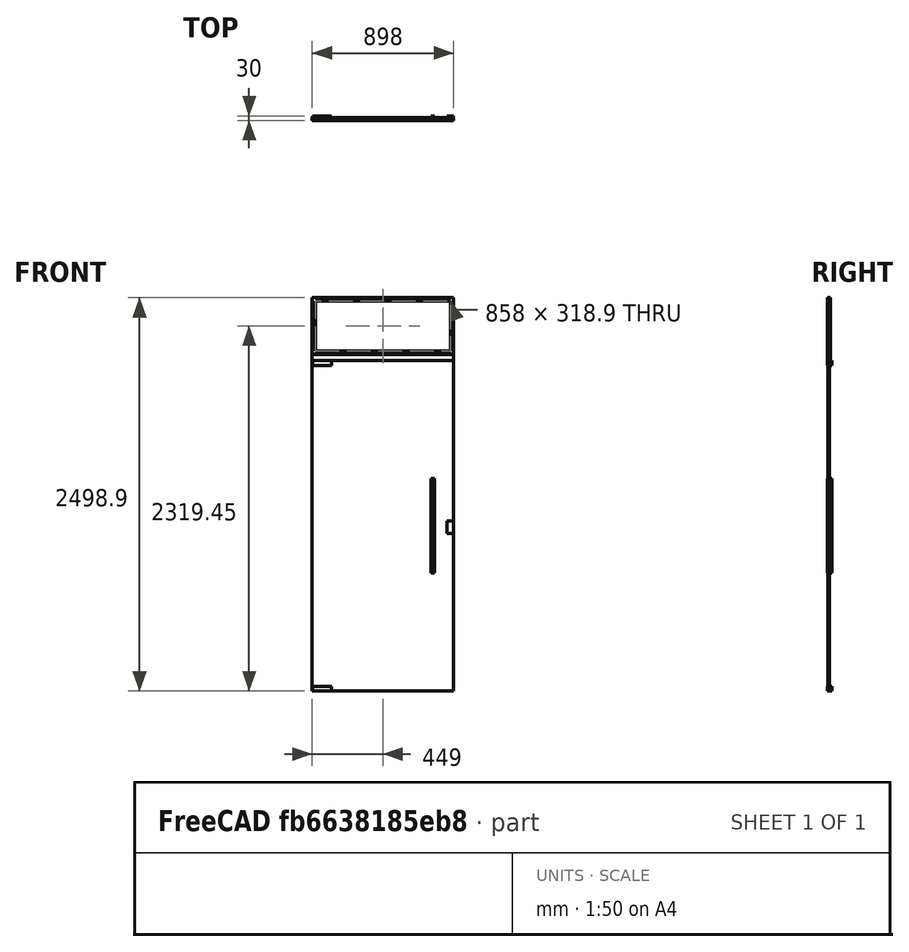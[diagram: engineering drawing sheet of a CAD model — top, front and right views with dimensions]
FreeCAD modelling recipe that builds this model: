
FCSTD DOCUMENT  (FreeCAD 0.16R6704 (Git))
Label: Simple glass door with handles and transom
License: CreativeCommons Attribution
LicenseURL: http://creativecommons.org/licenses/by/4.0/
objects: Sketcher::SketchObject×2, Part::FeaturePython×1, App::DocumentObjectGroup×1
note: 3 computed .brp shape members not serialized (recipe doc carries the construction recipe); baked Part::Feature solids carry a one-line shape summary decoded from their .brp

FEATURE [Sketcher::SketchObject] Sketch128
  Placement = pos=(0,0,0) rot=(1,0,0;1.5708rad)
  sketch-geometry (45):
    g0: LineSegment StartX=0 StartY=0 StartZ=0 EndX=900 EndY=0 EndZ=0
    g1: LineSegment StartX=900 StartY=2499.9 StartZ=0 EndX=0 EndY=2499.9 EndZ=0
    g2: LineSegment StartX=0 StartY=2499.9 StartZ=0 EndX=0 EndY=0 EndZ=0
    g3: LineSegment StartX=1 StartY=0 StartZ=0 EndX=899 EndY=0 EndZ=0
    g4: LineSegment StartX=899 StartY=0 StartZ=0 EndX=899 EndY=2100 EndZ=0
    g5: LineSegment StartX=899 StartY=2100 StartZ=0 EndX=1 EndY=2100 EndZ=0
    g6: LineSegment StartX=1 StartY=2100 StartZ=0 EndX=1 EndY=0 EndZ=0
    g7: LineSegment StartX=2 StartY=2099 StartZ=0 EndX=122 EndY=2099 EndZ=0
    g8: LineSegment StartX=122 StartY=2099 StartZ=0 EndX=122 EndY=2069 EndZ=0
    g9: LineSegment StartX=122 StartY=2069 StartZ=0 EndX=2 EndY=2069 EndZ=0
    g10: LineSegment StartX=2 StartY=2069 StartZ=0 EndX=2 EndY=2099 EndZ=0
    g11: LineSegment StartX=2 StartY=1 StartZ=0 EndX=122 EndY=1 EndZ=0
    g12: LineSegment StartX=122 StartY=1 StartZ=0 EndX=122 EndY=31 EndZ=0
    g13: LineSegment StartX=122 StartY=31 StartZ=0 EndX=2 EndY=31 EndZ=0
    g14: LineSegment StartX=2 StartY=31 StartZ=0 EndX=2 EndY=1 EndZ=0
    g15: LineSegment StartX=858 StartY=1080 StartZ=0 EndX=898 EndY=1080 EndZ=0
    g16: LineSegment StartX=898 StartY=1080 StartZ=0 EndX=898 EndY=1000 EndZ=0
    g17: LineSegment StartX=898 StartY=1000 StartZ=0 EndX=858 EndY=1000 EndZ=0
    g18: LineSegment StartX=858 StartY=1000 StartZ=0 EndX=858 EndY=1080 EndZ=0
    g19: LineSegment StartX=754 StartY=1350 StartZ=0 EndX=779 EndY=1350 EndZ=0
    g20: LineSegment StartX=779 StartY=1350 StartZ=0 EndX=779 EndY=750 EndZ=0
    g21: LineSegment StartX=779 StartY=750 StartZ=0 EndX=754 EndY=750 EndZ=0
    g22: LineSegment StartX=754 StartY=750 StartZ=0 EndX=754 EndY=1350 EndZ=0
    g23: LineSegment [constr] StartX=766.5 StartY=1477.64 StartZ=0 EndX=766.5 EndY=711 EndZ=0
    g24: Circle CenterX=766.5 CenterY=1335 CenterZ=0 NormalX=0 NormalY=0 NormalZ=1 Radius=5
    g25: Circle CenterX=766.5 CenterY=1050 CenterZ=0 NormalX=0 NormalY=0 NormalZ=1 Radius=5
    g26: Circle CenterX=766.5 CenterY=765 CenterZ=0 NormalX=0 NormalY=0 NormalZ=1 Radius=5
    g27: LineSegment [constr] StartX=712 StartY=1050 StartZ=0 EndX=790 EndY=1050 EndZ=0
    g28: LineSegment StartX=1 StartY=2498.9 StartZ=0 EndX=899 EndY=2498.9 EndZ=0
    g29: LineSegment StartX=899 StartY=2498.9 StartZ=0 EndX=899 EndY=2140 EndZ=0
    g30: LineSegment StartX=899 StartY=2140 StartZ=0 EndX=1 EndY=2140 EndZ=0
    g31: LineSegment StartX=1 StartY=2140 StartZ=0 EndX=1 EndY=2498.9 EndZ=0
    g32: LineSegment StartX=21 StartY=2478.9 StartZ=0 EndX=879 EndY=2478.9 EndZ=0
    g33: LineSegment StartX=879 StartY=2478.9 StartZ=0 EndX=879 EndY=2160 EndZ=0
    g34: LineSegment StartX=879 StartY=2160 StartZ=0 EndX=21 EndY=2160 EndZ=0
    g35: LineSegment StartX=21 StartY=2160 StartZ=0 EndX=21 EndY=2478.9 EndZ=0
    g36: LineSegment StartX=900 StartY=2499.9 StartZ=0 EndX=900 EndY=0 EndZ=0
    g37: LineSegment StartX=-0.1 StartY=2500 StartZ=0 EndX=900.1 EndY=2500 EndZ=0
    g38: LineSegment StartX=900.1 StartY=2500 StartZ=0 EndX=900.1 EndY=0 EndZ=0
    g39: LineSegment StartX=900.1 StartY=0 StartZ=0 EndX=-0.1 EndY=0 EndZ=0
    g40: LineSegment StartX=-0.1 StartY=0 StartZ=0 EndX=-0.1 EndY=2500 EndZ=0
    g41: LineSegment StartX=1 StartY=2139 StartZ=0 EndX=899 EndY=2139 EndZ=0
    g42: LineSegment StartX=899 StartY=2139 StartZ=0 EndX=899 EndY=2101 EndZ=0
    g43: LineSegment StartX=899 StartY=2101 StartZ=0 EndX=1 EndY=2101 EndZ=0
    g44: LineSegment StartX=1 StartY=2101 StartZ=0 EndX=1 EndY=2139 EndZ=0
  constraints (132):
    c: Coincident(g1,g2)
    c: Coincident(g2,g0)
    c: Horizontal(g0)
    c: Horizontal(g1)
    c: Vertical(g2)
    c: Coincident(g3,g4)
    c: Coincident(g4,g5)
    c: Coincident(g5,g6)
    c: Coincident(g6,g3)
    c: Horizontal(g3)
    c: Horizontal(g5)
    c: Vertical(g4)
    c: Vertical(g6)
    c: DistanceX(g0) = 900  'Largura do vão'
    c: DistanceX(g1,g5) = 1
    c: DistanceX(g3,g0) = 1
    c: DistanceY(g0,g3) = 0
    c: Coincident(g0,g-1)
    c: Coincident(g7,g8)
    c: Coincident(g8,g9)
    c: Coincident(g9,g10)
    c: Coincident(g10,g7)
    c: Horizontal(g7)
    c: Horizontal(g9)
    c: Vertical(g8)
    c: Vertical(g10)
    c: Coincident(g11,g12)
    c: Coincident(g12,g13)
    c: Coincident(g13,g14)
    c: Coincident(g14,g11)
    c: Horizontal(g11)
    c: Horizontal(g13)
    c: Vertical(g12)
    c: Vertical(g14)
    c: Coincident(g15,g16)
    c: Coincident(g16,g17)
    c: Coincident(g17,g18)
    c: Coincident(g18,g15)
    c: Horizontal(g15)
    c: Horizontal(g17)
    c: Vertical(g16)
    c: Vertical(g18)
    c: DistanceX(g5,g7) = 1
    c: DistanceY(g8,g7) = 30  'Altura do apoio'
    c: DistanceX(g9,g8) = 120  'Largura do apoio'
    c: Equal(g8,g12)
    c: Equal(g13,g7)
    c: DistanceX(g3,g11) = 1
    c: DistanceY(g3,g11) = 1
    c: DistanceX(g16,g3) = 1
    c: DistanceY(g17,g15) = 80  'Altura da tranca'
    c: DistanceX(g15,g15) = 40  'Largura da tranca'
    c: DistanceY(g3,g17) = 1000  'Altura tranca ao chão'
    c: Coincident(g19,g20)
    c: Coincident(g20,g21)
    c: Coincident(g21,g22)
    c: Coincident(g22,g19)
    c: Horizontal(g19)
    c: Horizontal(g21)
    c: Vertical(g20)
    c: Vertical(g22)
    c: DistanceX(g19,g19) = 25  'Largura puxador'
    c: DistanceY(g20,g19) = 600  'Altura do puxador'
    c: Vertical(g23)  'Constraint69'
    c: Symmetric(g19,g19,g23)  'Constraint68'
    c: PointOnObject(g24,g23)  'Constraint72'
    c: PointOnObject(g25,g23)  'Constraint71'
    c: PointOnObject(g26,g23)  'Constraint70'
    c: Radius(g26) = 5  'Apoio puxador'
    c: Equal(g26,g25)  'Constraint83'
    c: Equal(g26,g24)  'Constraint82'
    c: DistanceY(g24,g19) = 15  'Constraint73'
    c: DistanceY(g20,g26) = 15
    c: Horizontal(g27)
    c: PointOnObject(g25,g27)
    c: Symmetric(g21,g19,g27)
    c: DistanceY(g3,g20) = 750  'Distância do puxador ao solo'
    c: DistanceX(g20,g3) = 120  'Distância do puxador'
    c: Coincident(g28,g29)  'Constraint79'
    c: Coincident(g29,g30)
    c: Coincident(g30,g31)
    c: Coincident(g31,g28)
    c: Horizontal(g28)
    c: Horizontal(g30)
    c: Vertical(g29)
    c: Vertical(g31)
    c: Coincident(g32,g33)
    c: Coincident(g33,g34)
    c: Coincident(g34,g35)
    c: Coincident(g35,g32)
    c: Horizontal(g32)
    c: Horizontal(g34)
    c: Vertical(g33)
    c: Vertical(g35)
    c: DistanceX(g28,g32) = 20
    c: DistanceY(g32,g28) = 20
    c: DistanceX(g32,g28) = 20
    c: DistanceY(g29,g33) = 20
    c: DistanceX(g29,g4) = 0
    c: DistanceX(g30,g5) = 0
    c: Coincident(g36,g1)
    c: Coincident(g36,g0)
    c: Vertical(g36)
    c: DistanceY(g-1,g5) = 2100  'Altura da porta'
    c: DistanceY(g5,g30) = 40  'Altura do perfil bandeira'
    c: DistanceY(g28,g1) = 1
    c: Coincident(g37,g38)
    c: Coincident(g38,g39)
    c: Coincident(g39,g40)
    c: Coincident(g40,g37)
    c: Horizontal(g37)
    c: Horizontal(g39)
    c: Vertical(g38)
    c: Vertical(g40)
    c: DistanceX(g37,g1) = 0.1
    c: DistanceY(g1,g37) = 0.1
    c: DistanceX(g1,g37) = 0.1
    c: DistanceY(g5,g37) = 400  'Altura bandeira'
    c: DistanceY(g39,g-1) = 0
    c: Coincident(g41,g42)
    c: Coincident(g42,g43)
    c: Coincident(g43,g44)
    c: Coincident(g44,g41)
    c: Horizontal(g41)
    c: Horizontal(g43)
    c: Vertical(g42)
    c: Vertical(g44)
    c: DistanceX(g30,g41) = 0
    c: DistanceY(g41,g30) = 1
    c: DistanceY(g5,g43) = 1
    c: DistanceX(g41,g29) = 0
    c: DistanceY(g7,g5) = 1
FEATURE [Part::FeaturePython] Window092  label="Simple glass door with handles and transom "  # WARN: FeaturePython — macro-defined, semantics opaque (R4)
  Base = -> Sketch128
  Height = 2100
  HoleDepth = 0
  MoveWithHost = true
  Normal = (0,1,0)
  Preset = 6
  Role = 1
  Width = 900
  WindowParts = PORTA DE VIDRO | Glass panel | Wire1 | 10.0 | 5.0 | APOIO SUPERIOR | Frame | Wire2 | 30.0 | 0.0 | APOIO INFERIOR | Frame | Wire3 | 30.0 | 0.0 | TRANCA | Frame | Wire4 | 30.0 | 0.0 | PUXADOR 1 | Frame | Wire5 | 10.0 | 0.0 | PUXADOR 2 | Frame | Wire5 | 10.0 | 20.0 | APOIO SUPERIOR PUXADOR | Frame | Wire6 | 30.0 | 0.0 | APOIO CENTRAL PUXADOR | Frame | Wire7 | 30.0 | 0.0 | APOIO INFERIOR PUXADOR | Frame | Wire8 | 30.0 | 0.0 | PERFIL | Frame | Wire10,Wire9 | 20.0 | 0.0 | VIDRO SUPERIOR | Glass panel | Wire10 | 10.0 | 5.0 | PERFIL BANDEIRA | Frame | Wire12 | 20.0 | 0.0
FEATURE [Sketcher::SketchObject] Sketch129  label="Opening indication "
  ExternalGeometry = -> [Window092]
  Placement = pos=(0,5,0) rot=(1,0,0;1.5708rad)
  Support = -> Window092 [Face5]
  sketch-geometry (6):
    g0: LineSegment [constr] StartX=-528.499 StartY=1038.78 StartZ=0 EndX=1595.51 EndY=1038.78 EndZ=0
    g1: LineSegment StartX=56 StartY=2100 StartZ=0 EndX=1 EndY=1038.78 EndZ=0
    g2: LineSegment StartX=1 StartY=1038.78 StartZ=0 EndX=56 EndY=0 EndZ=0
    g3: LineSegment StartX=56 StartY=0 StartZ=0 EndX=899 EndY=1037 EndZ=0
    g4: LineSegment StartX=899 StartY=1037 StartZ=0 EndX=56 EndY=2100 EndZ=0
    g5: LineSegment [constr] StartX=56 StartY=2303.39 StartZ=0 EndX=56 EndY=-131.026 EndZ=0
  constraints (15):
    c: Horizontal(g0)
    c: DistanceY(g-6,g0) = 1038.78  'Altura tranca'
    c: PointOnObject(g1,g-3)
    c: PointOnObject(g1,g0)
    c: Coincident(g1,g2)
    c: PointOnObject(g2,g-6)
    c: Coincident(g2,g3)
    c: PointOnObject(g3,g-5)
    c: Coincident(g3,g4)
    c: Coincident(g4,g1)
    c: Vertical(g5)
    c: PointOnObject(g2,g5)
    c: PointOnObject(g1,g5)
    c: PointOnObject(g1,g-4)
    c: DistanceX(g-6,g5) = 55  'Door_axis'
FEATURE [App::DocumentObjectGroup] Grupo099  label="Simple glass door with handles and transom"
  Group = -> [Window092,Sketch129]
